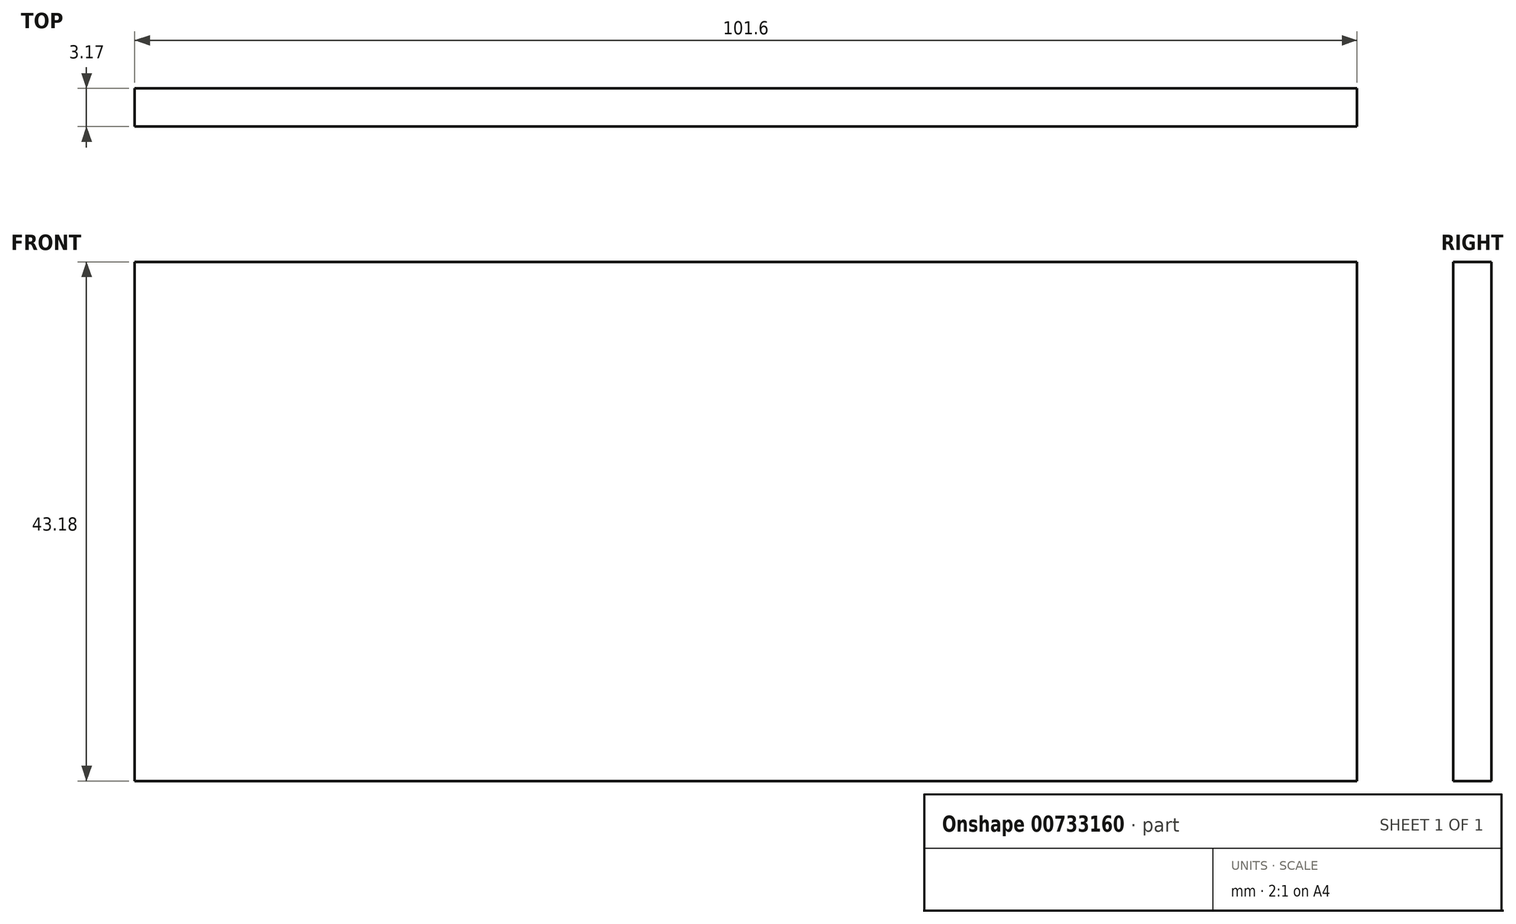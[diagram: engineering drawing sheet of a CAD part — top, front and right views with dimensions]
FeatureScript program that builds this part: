
annotation { "Feature Type Name" : "Feature", "Feature Type Description" : "" }
export const myFeature = defineFeature(function(context is Context, id is Id, definition is map)
    precondition{}
    {
        {
            var Q0;
            Q0=qCreatedBy(makeId("Front.planeOp"),FACE);
            var sketch = newSketch(context, id + "F0", { "sketchPlane" : qUnion([Q0])});
            skLineSegment(sketch, "E0.bottom", {"start": v(0, 0) * mm, "end": v(101.6, 0) * mm});
            skLineSegment(sketch, "E0.top", {"start": v(0, 43.18) * mm, "end": v(101.6, 43.18) * mm});
            skLineSegment(sketch, "E0.left", {"start": v(0, 0) * mm, "end": v(0, 43.18) * mm});
            skLineSegment(sketch, "E0.right", {"start": v(101.6, 0) * mm, "end": v(101.6, 43.18) * mm});
            skSolve(sketch);
        }
        {
            var Q0;
            Q0 = qSketchRegion(id + "F0", true);
            extrude(context, id + "F1", {"entities" : qUnion([Q0]), "depth" : 3.17 * mm, "offsetDistance" : 25.4 * mm});
        }
    });
